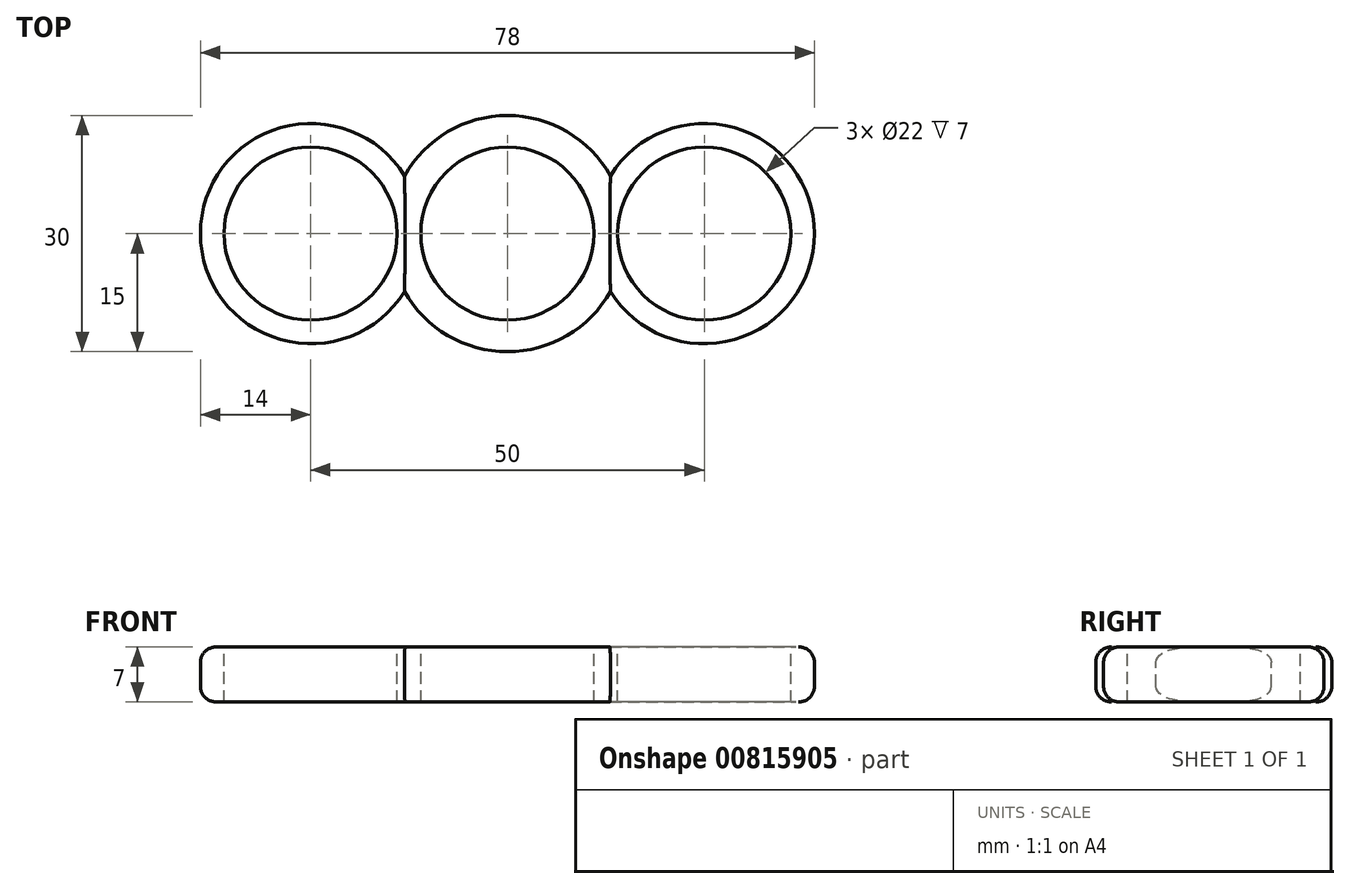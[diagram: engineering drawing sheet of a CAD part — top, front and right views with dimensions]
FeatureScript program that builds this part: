
annotation { "Feature Type Name" : "Feature", "Feature Type Description" : "" }
export const myFeature = defineFeature(function(context is Context, id is Id, definition is map)
    precondition{}
    {
        {
            var Q0;
            Q0=qCreatedBy(makeId("Top.planeOp"),FACE);
            var sketch = newSketch(context, id + "F0", { "sketchPlane" : qUnion([Q0])});
            skCircle(sketch, "E0", {"center": v(0, 0) * mm, "radius": 11 * mm});
            skLineSegment(sketch, "E1", {"start": v(0, 0) * mm, "end": v(25, 0) * mm});
            skCircle(sketch, "E2", {"center": v(-25, 0) * mm, "radius": 11 * mm});
            skCircle(sketch, "E3", {"center": v(25, 0) * mm, "radius": 11 * mm});
            skArc(sketch, "E4", {"start": v(-13.08, 7.34) * mm, "mid": v(-39, 0) * mm, "end": v(-13.08, -7.34) * mm});
            skArc(sketch, "E5", {"start": v(13.08, -7.34) * mm, "mid": v(39, 0) * mm, "end": v(13.08, 7.34) * mm});
            skArc(sketch, "E6", {"start": v(-13.08, -7.34) * mm, "mid": v(0, -15) * mm, "end": v(13.08, -7.34) * mm});
            skArc(sketch, "E7.trimOffspring", {"start": v(13.08, 7.34) * mm, "mid": v(0, 15) * mm, "end": v(-13.08, 7.34) * mm});
            skSolve(sketch);
        }
        {
            var Q0;
            Q0=makeQuery(id+"F0.imprint","IMPRINT",FACE,{"disambiguationData":[TD([[makeQuery(id+"F0.imprint","IMPRINT",EDGE,{"derivedFrom":sQuery(id+"F0.wireOp",EDGE,"E0")}),-1.0]])]});
            extrude(context, id + "F1", {"entities" : qUnion([Q0]), "oppositeDirection" : true, "depth" : 7 * mm, "offsetDistance" : 25 * mm});
        }
        {
            var Q0;
            Q0=makeQuery(id+"F1.opExtrude","CAP_EDGE",EDGE,{"disambiguationData":[OSD([sQuery(id+"F0.wireOp",EDGE,"E4")])],"isStart":true});
            var Q1;
            Q1=makeQuery(id+"F1.opExtrude","CAP_EDGE",EDGE,{"disambiguationData":[OSD([sQuery(id+"F0.wireOp",EDGE,"E7.trimOffspring")])],"isStart":true});
            var Q2;
            Q2=makeQuery(id+"F1.opExtrude","CAP_EDGE",EDGE,{"disambiguationData":[OSD([sQuery(id+"F0.wireOp",EDGE,"E5")])],"isStart":true});
            var Q3;
            Q3=makeQuery(id+"F1.opExtrude","CAP_EDGE",EDGE,{"disambiguationData":[OSD([sQuery(id+"F0.wireOp",EDGE,"E6")])],"isStart":true});
            var Q4;
            Q4=makeQuery(id+"F1.opExtrude","CAP_EDGE",EDGE,{"disambiguationData":[OSD([sQuery(id+"F0.wireOp",EDGE,"E4")])],"isStart":false});
            var Q5;
            Q5=makeQuery(id+"F1.opExtrude","CAP_EDGE",EDGE,{"disambiguationData":[OSD([sQuery(id+"F0.wireOp",EDGE,"E6")])],"isStart":false});
            var Q6;
            Q6=makeQuery(id+"F1.opExtrude","CAP_EDGE",EDGE,{"disambiguationData":[OSD([sQuery(id+"F0.wireOp",EDGE,"E5")])],"isStart":false});
            var Q7;
            Q7=makeQuery(id+"F1.opExtrude","CAP_EDGE",EDGE,{"disambiguationData":[OSD([sQuery(id+"F0.wireOp",EDGE,"E7.trimOffspring")])],"isStart":false});
            fillet(context, id + "F2", {"entities" : qUnion([Q0, Q1, Q2, Q3, Q4, Q5, Q6, Q7]), "radius" : 2 * mm, "tangentPropagation" : true, "allowEdgeOverflow" : false});
        }
    });
